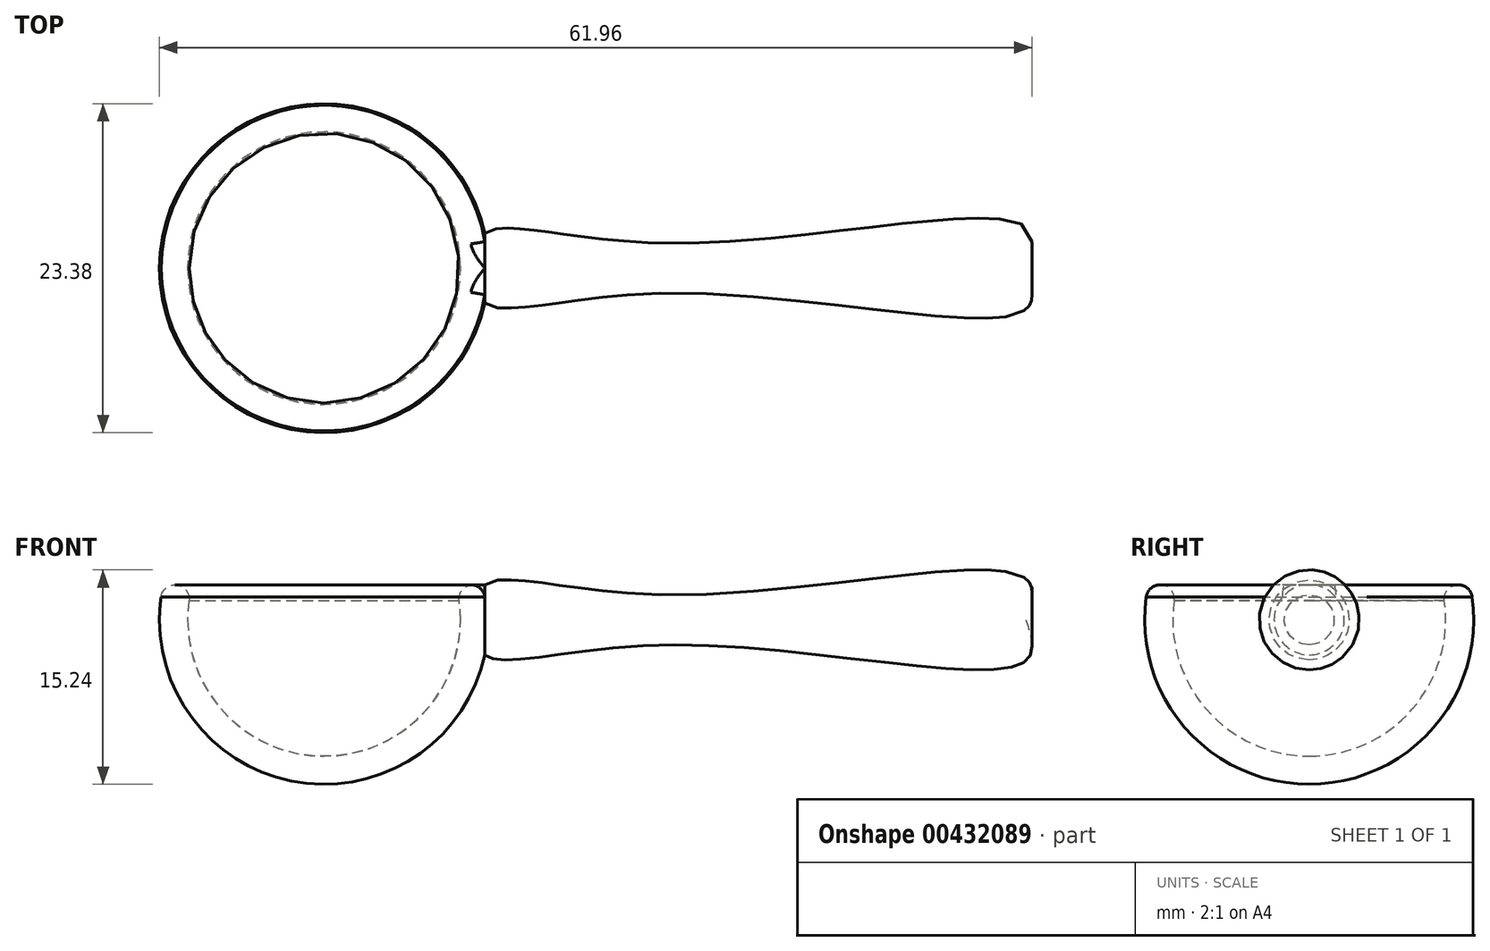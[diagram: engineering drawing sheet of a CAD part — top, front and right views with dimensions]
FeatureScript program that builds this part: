
annotation { "Feature Type Name" : "Feature", "Feature Type Description" : "" }
export const myFeature = defineFeature(function(context is Context, id is Id, definition is map)
    precondition{}
    {
        {
            var Q0;
            Q0=qCreatedBy(makeId("Front.planeOp"),FACE);
            var sketch = newSketch(context, id + "F0", { "sketchPlane" : qUnion([Q0])});
            skFitSpline(sketch, "E0", {"points": [v(49.85, 0) * mm, v(49.74, -3) * mm, v(24.6, -1.78) * mm, v(11.42, -2.5) * mm, v(11.11, 0) * mm], "startDerivative": vector(8, -24.75) * mm, "endDerivative": vector(2.98, 22.87) * mm});
            skCircle(sketch, "E1", {"center": v(0, 0) * mm, "radius": 11.69 * mm});
            skLineSegment(sketch, "E2", {"start": v(11.69, 0) * mm, "end": v(-11.69, 0) * mm});
            skLineSegment(sketch, "E3", {"start": v(11.11, 0) * mm, "end": v(49.85, 0) * mm});
            skLineSegment(sketch, "E4", {"start": v(11.42, -2.5) * mm, "end": v(11.42, 2.5) * mm});
            skLineSegment(sketch, "E5", {"start": v(11.42, 2.5) * mm, "end": v(-11.42, 2.5) * mm});
            skSolve(sketch);
        }
        {
            var Q0;
            {var subQ0=sQuery(id+"F0.wireOp",EDGE,"E2");Q0=makeQuery(id+"F0.imprint","IMPRINT",FACE,{"disambiguationData":[TD([[makeQuery(id+"F0.imprint","IMPRINT",EDGE,{"derivedFrom":subQ0}),1.0]])]});}
            var Q1;
            {var subQ0=sQuery(id+"F0.wireOp",EDGE,"E3");var subQ3=sQuery(id+"F0.wireOp",EDGE,"E4");var subQ5=makeQuery(id+"F0.imprint","INTERSECT",VERTEX,{"derivedFrom":[subQ0,subQ3]});Q1=makeQuery(id+"F0.imprint","IMPRINT",FACE,{"disambiguationData":[TD([[makeQuery(id+"F0.imprint","IMPRINT",EDGE,{"disambiguationData":[TD([[subQ5,1.0]])],"derivedFrom":subQ0}),-1.0]])]});}
            var Q2;
            {var subQ1=sQuery(id+"F0.wireOp",EDGE,"E1");var subQ3=sQuery(id+"F0.wireOp",EDGE,"E3");var subQ4=makeQuery(id+"F0.imprint","INTERSECT",VERTEX,{"derivedFrom":[subQ1,subQ3]});Q2=makeQuery(id+"F0.imprint","IMPRINT",FACE,{"disambiguationData":[TD([[makeQuery(id+"F0.imprint","IMPRINT",EDGE,{"disambiguationData":[TD([[subQ4,1.0]])],"derivedFrom":subQ3}),-1.0]])]});}
            var Q3;
            {var subQ0=sQuery(id+"F0.wireOp",EDGE,"E3");var subQ1=sQuery(id+"F0.wireOp",EDGE,"E0");var subQ2=makeQuery(id+"F0.imprint","INTERSECT",VERTEX,{"derivedFrom":[subQ1,subQ0]});Q3=makeQuery(id+"F0.imprint","IMPRINT",FACE,{"disambiguationData":[TD([[makeQuery(id+"F0.imprint","IMPRINT",EDGE,{"disambiguationData":[TD([[subQ2,1.0]])],"derivedFrom":subQ0}),-1.0]])]});}
            var Q4;
            Q4=sQuery(id+"F0.wireOp",EDGE,"E2");
            revolve(context, id + "F1", {"entities" : qUnion([Q0, Q1, Q2, Q3]), "axis" : qUnion([Q4]), "revolveType" : RevolveType.FULL});
        }
        {
            var Q0;
            {var subQ0=sQuery(id+"F0.wireOp",EDGE,"E5");Q0=makeQuery(id+"F0.imprint","IMPRINT",FACE,{"disambiguationData":[TD([[makeQuery(id+"F0.imprint","IMPRINT",EDGE,{"derivedFrom":subQ0}),-1.0]])]});}
            extrude(context, id + "F2", {"entities" : qUnion([Q0]), "operationType" : NewBodyOperationType.REMOVE, "endBound" : BoundingType.SYMMETRIC, "oppositeDirection" : true, "depth" : 25 * mm});
        }
        {
            var Q0;
            Q0=makeQuery(id+"F2.boolean.opBoolean","COPY",FACE,{"derivedFrom":makeQuery(id+"F2.opExtrude","SWEPT_FACE",FACE,{"disambiguationData":[OSD([sQuery(id+"F0.wireOp",EDGE,"E5")])]})});
            shell(context, id + "F3", {"entities" : qUnion([Q0]), "thickness" : 2 * mm});
        }
        {
            var Q0;
            Q0=makeQuery(id+"F2.boolean.opBoolean","INTERSECT",EDGE,{"derivedFrom":[makeQuery(id+"F1.opRevolve","SWEPT_FACE",FACE,{"disambiguationData":[OSD([sQuery(id+"F0.wireOp",EDGE,"E1")])]}),makeQuery(id+"F2.opExtrude","SWEPT_FACE",FACE,{"disambiguationData":[OSD([sQuery(id+"F0.wireOp",EDGE,"E5")])]})]});
            var Q1;
            Q1=makeQuery(id+"F3.opShell","OFFSET_EDGE",EDGE,{"disambiguationData":[OSD([sQuery(id+"F0.wireOp",EDGE,"E1"),sQuery(id+"F0.wireOp",EDGE,"E5")])]});
            fillet(context, id + "F4", {"entities" : qUnion([Q0, Q1]), "radius" : 1 * mm, "tangentPropagation" : true, "allowEdgeOverflow" : false});
        }
    });
